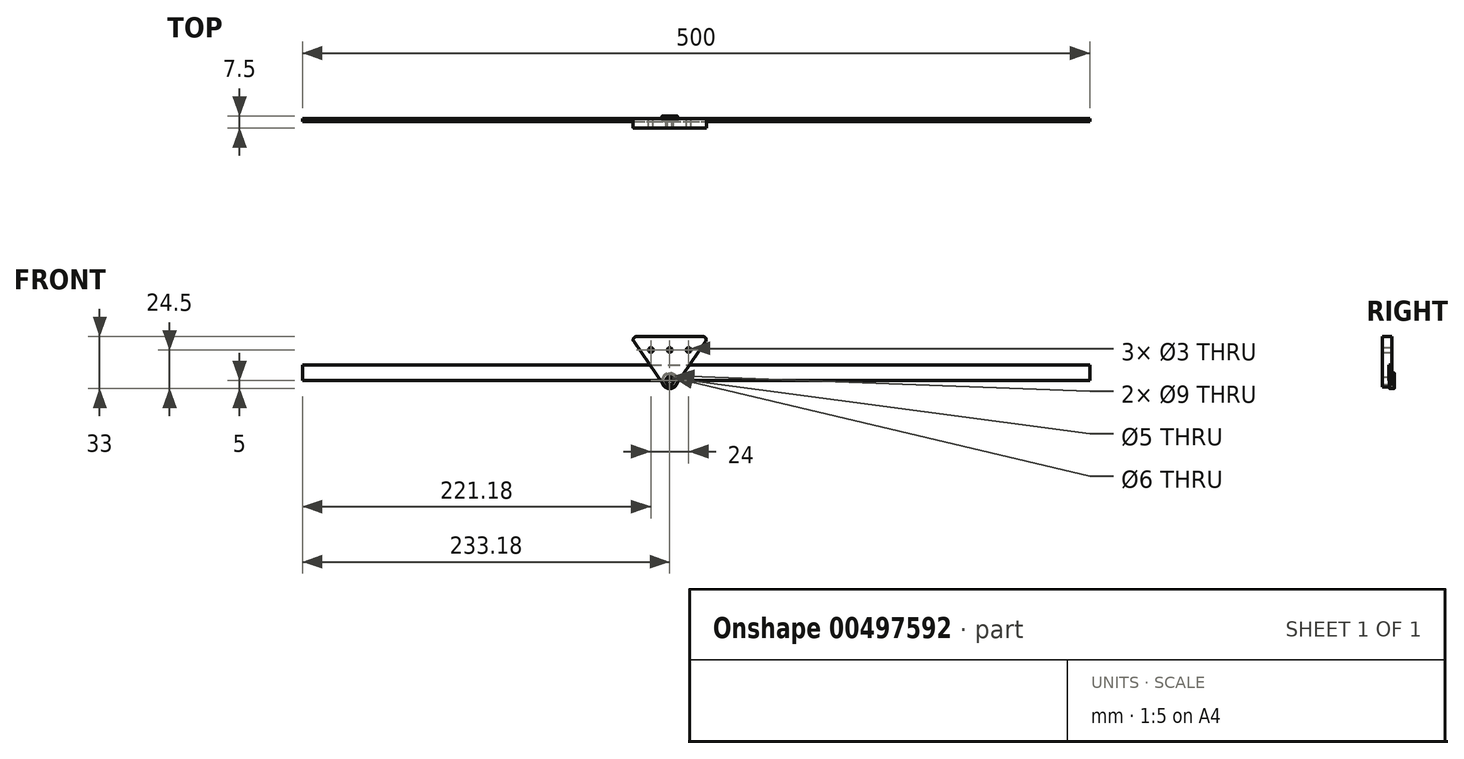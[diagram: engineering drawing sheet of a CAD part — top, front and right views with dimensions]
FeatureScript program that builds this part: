
annotation { "Feature Type Name" : "Feature", "Feature Type Description" : "" }
export const myFeature = defineFeature(function(context is Context, id is Id, definition is map)
    precondition{}
    {
        {
            var Q0;
            Q0=qCreatedBy(makeId("Right.planeOp"),FACE);
            var sketch = newSketch(context, id + "F0", { "sketchPlane" : qUnion([Q0])});
            skLineSegment(sketch, "E0", {"start": v(-1.43, 3.5) * mm, "end": v(-1.47, 3.5) * mm});
            skLineSegment(sketch, "E1", {"start": v(-1.5, 3.47) * mm, "end": v(-1.5, 3.05) * mm});
            skLineSegment(sketch, "E2", {"start": v(-1.45, 3) * mm, "end": v(0, 3) * mm});
            skPoint(sketch, "E3.visualSharp", {"position": v(-1.5, 3) * mm});
            skArc(sketch, "E3.filletArc", {"start": v(-1.5, 3.05) * mm, "mid": v(-1.49, 3.01) * mm, "end": v(-1.45, 3) * mm});
            skPoint(sketch, "E4.visualSharp", {"position": v(-1.5, 3.5) * mm});
            skArc(sketch, "E4.filletArc", {"start": v(-1.47, 3.5) * mm, "mid": v(-1.5, 3.5) * mm, "end": v(-1.5, 3.47) * mm});
            skPoint(sketch, "E5.visualSharp", {"position": v(-1.33, 3.5) * mm});
            skLineSegment(sketch, "E6", {"start": v(-1.33, 4) * mm, "end": v(0.6, 4) * mm, "construction": true});
            skLineSegment(sketch, "E7", {"start": v(-1.33, 3.6) * mm, "end": v(-1.33, 4) * mm});
            skLineSegment(sketch, "E8", {"start": v(-1.33, 3.6) * mm, "end": v(-1.33, 3.53) * mm});
            skLineSegment(sketch, "E9", {"start": v(-1.43, 3.5) * mm, "end": v(-1.36, 3.5) * mm});
            skArc(sketch, "E10.filletArc", {"start": v(-1.36, 3.5) * mm, "mid": v(-1.34, 3.5) * mm, "end": v(-1.33, 3.53) * mm});
            skArc(sketch, "E11.MirrorCS", {"start": v(-1.36, 4.5) * mm, "mid": v(-1.34, 4.5) * mm, "end": v(-1.33, 4.47) * mm});
            skLineSegment(sketch, "E12.MirrorCS", {"start": v(-1.43, 4.5) * mm, "end": v(-1.36, 4.5) * mm});
            skLineSegment(sketch, "E13.MirrorCS", {"start": v(-1.33, 4.4) * mm, "end": v(-1.33, 4.47) * mm});
            skArc(sketch, "E14.MirrorCS", {"start": v(-1.47, 4.5) * mm, "mid": v(-1.5, 4.5) * mm, "end": v(-1.5, 4.53) * mm});
            skLineSegment(sketch, "E15.MirrorCS", {"start": v(-1.43, 4.5) * mm, "end": v(-1.47, 4.5) * mm});
            skArc(sketch, "E16.MirrorCS", {"start": v(-1.5, 4.95) * mm, "mid": v(-1.49, 4.99) * mm, "end": v(-1.45, 5) * mm});
            skPoint(sketch, "E17.MirrorP", {"position": v(-1.33, 4.5) * mm});
            skLineSegment(sketch, "E18.MirrorCS", {"start": v(-1.5, 4.53) * mm, "end": v(-1.5, 4.95) * mm});
            skLineSegment(sketch, "E19.MirrorCS", {"start": v(-1.33, 4.4) * mm, "end": v(-1.33, 4) * mm});
            skPoint(sketch, "E20.MirrorP", {"position": v(-1.5, 5) * mm});
            skPoint(sketch, "E21.MirrorP", {"position": v(-1.5, 4.5) * mm});
            skLineSegment(sketch, "E22", {"start": v(-1.45, 5) * mm, "end": v(0, 5) * mm});
            skLineSegment(sketch, "E23", {"start": v(-5.2, 0) * mm, "end": v(6.02, 0) * mm, "construction": true});
            skLineSegment(sketch, "E24", {"start": v(0, 6.2) * mm, "end": v(0, 1.5) * mm, "construction": true});
            skLineSegment(sketch, "E25.MirrorCS", {"start": v(1.33, 4.4) * mm, "end": v(1.33, 4.47) * mm});
            skArc(sketch, "E26.MirrorCS", {"start": v(1.36, 4.5) * mm, "mid": v(1.34, 4.5) * mm, "end": v(1.33, 4.47) * mm});
            skLineSegment(sketch, "E27.MirrorCS", {"start": v(1.43, 4.5) * mm, "end": v(1.36, 4.5) * mm});
            skLineSegment(sketch, "E28.MirrorCS", {"start": v(1.33, 3.6) * mm, "end": v(1.33, 3.53) * mm});
            skLineSegment(sketch, "E29.MirrorCS", {"start": v(1.43, 3.5) * mm, "end": v(1.36, 3.5) * mm});
            skArc(sketch, "E30.MirrorCS", {"start": v(1.36, 3.5) * mm, "mid": v(1.34, 3.5) * mm, "end": v(1.33, 3.53) * mm});
            skLineSegment(sketch, "E31.MirrorCS", {"start": v(1.43, 3.5) * mm, "end": v(1.47, 3.5) * mm});
            skArc(sketch, "E32.MirrorCS", {"start": v(1.47, 3.5) * mm, "mid": v(1.5, 3.5) * mm, "end": v(1.5, 3.47) * mm});
            skLineSegment(sketch, "E33.MirrorCS", {"start": v(1.43, 4.5) * mm, "end": v(1.47, 4.5) * mm});
            skArc(sketch, "E34.MirrorCS", {"start": v(1.47, 4.5) * mm, "mid": v(1.5, 4.5) * mm, "end": v(1.5, 4.53) * mm});
            skArc(sketch, "E35.MirrorCS", {"start": v(1.5, 3.05) * mm, "mid": v(1.49, 3.01) * mm, "end": v(1.45, 3) * mm});
            skArc(sketch, "E36.MirrorCS", {"start": v(1.5, 4.95) * mm, "mid": v(1.49, 4.99) * mm, "end": v(1.45, 5) * mm});
            skPoint(sketch, "E37.MirrorP", {"position": v(1.33, 3.5) * mm});
            skPoint(sketch, "E38.MirrorP", {"position": v(1.33, 4.5) * mm});
            skLineSegment(sketch, "E39.MirrorCS", {"start": v(1.33, 3.6) * mm, "end": v(1.33, 4) * mm});
            skLineSegment(sketch, "E40.MirrorCS", {"start": v(1.45, 3) * mm, "end": v(0, 3) * mm});
            skLineSegment(sketch, "E41.MirrorCS", {"start": v(1.5, 3.47) * mm, "end": v(1.5, 3.05) * mm});
            skPoint(sketch, "E42.MirrorP", {"position": v(1.5, 3.5) * mm});
            skPoint(sketch, "E43.MirrorP", {"position": v(1.5, 3) * mm});
            skLineSegment(sketch, "E44.MirrorCS", {"start": v(1.45, 5) * mm, "end": v(0, 5) * mm});
            skLineSegment(sketch, "E45.MirrorCS", {"start": v(1.5, 4.53) * mm, "end": v(1.5, 4.95) * mm});
            skLineSegment(sketch, "E46.MirrorCS", {"start": v(1.33, 4.4) * mm, "end": v(1.33, 4) * mm});
            skPoint(sketch, "E47.MirrorP", {"position": v(1.5, 5) * mm});
            skPoint(sketch, "E48.MirrorP", {"position": v(1.5, 4.5) * mm});
            skLineSegment(sketch, "E49.MirrorCS", {"start": v(1.33, 4) * mm, "end": v(-0.6, 4) * mm, "construction": true});
            skSolve(sketch);
        }
        {
            var Q0;
            Q0=qSketchRegion(id+"F0",true);
            var Q1;
            Q1=sQuery(id+"F0.wireOp",EDGE,"E23");
            revolve(context, id + "F1", {"surfaceOperationType" : NewSurfaceOperationType.NEW, "entities" : qUnion([Q0]), "axis" : qUnion([Q1]), "revolveType" : RevolveType.FULL});
        }
        {
            var Q0;
            Q0=qCreatedBy(makeId("Front.planeOp"),FACE);
            var sketch = newSketch(context, id + "F2", { "sketchPlane" : qUnion([Q0])});
            skLineSegment(sketch, "E50", {"start": v(21.08, -5) * mm, "end": v(-21.47, -5) * mm, "construction": true});
            skLineSegment(sketch, "E51", {"start": v(0, -5) * mm, "end": v(0, 28) * mm, "construction": true});
            skLineSegment(sketch, "E52", {"start": v(0, 28) * mm, "end": v(-21.2, 28) * mm});
            skLineSegment(sketch, "E53", {"start": v(-1.95, -4) * mm, "end": v(0, -4) * mm});
            skLineSegment(sketch, "E54", {"start": v(-22.85, 24.87) * mm, "end": v(-3.6, -3.13) * mm});
            skLineSegment(sketch, "E55.MirrorCS", {"start": v(1.95, -4) * mm, "end": v(0, -4) * mm});
            skLineSegment(sketch, "E56.MirrorCS", {"start": v(0, 28) * mm, "end": v(21.2, 28) * mm});
            skLineSegment(sketch, "E57.MirrorCS", {"start": v(22.85, 24.87) * mm, "end": v(3.6, -3.13) * mm});
            skCircle(sketch, "E58", {"center": v(0, 0) * mm, "radius": 2.5 * mm});
            skCircle(sketch, "E59", {"center": v(0, 19.5) * mm, "radius": 1.5 * mm});
            skCircle(sketch, "E60", {"center": v(-12, 19.5) * mm, "radius": 1.5 * mm});
            skCircle(sketch, "E61.MirrorC", {"center": v(12, 19.5) * mm, "radius": 1.5 * mm});
            skPoint(sketch, "E62.visualSharp", {"position": v(-25, 28) * mm});
            skArc(sketch, "E62.filletArc", {"start": v(-21.2, 28) * mm, "mid": v(-22.97, 26.93) * mm, "end": v(-22.85, 24.87) * mm});
            skPoint(sketch, "E63.visualSharp", {"position": v(25, 28) * mm});
            skArc(sketch, "E63.filletArc", {"start": v(22.85, 24.87) * mm, "mid": v(22.97, 26.93) * mm, "end": v(21.2, 28) * mm});
            skPoint(sketch, "E64.visualSharp", {"position": v(3, -4) * mm});
            skArc(sketch, "E64.filletArc", {"start": v(1.95, -4) * mm, "mid": v(2.88, -3.77) * mm, "end": v(3.6, -3.13) * mm});
            skPoint(sketch, "E65.visualSharp", {"position": v(-3, -4) * mm});
            skArc(sketch, "E65.filletArc", {"start": v(-3.6, -3.13) * mm, "mid": v(-2.88, -3.77) * mm, "end": v(-1.95, -4) * mm});
            skSolve(sketch);
        }
        {
            var Q0;
            Q0=makeQuery(id+"F2.imprint","IMPRINT",FACE,{"disambiguationData":[TD([[makeQuery(id+"F2.imprint","IMPRINT",EDGE,{"derivedFrom":sQuery(id+"F2.wireOp",EDGE,"E52")}),1.0]])]});
            extrude(context, id + "F3", {"entities" : qUnion([Q0]), "depth" : 6 * mm, "offsetDistance" : 25 * mm});
        }
        {
            var Q0;
            Q0=qCreatedBy(makeId("Front.planeOp"),FACE);
            var sketch = newSketch(context, id + "F4", { "sketchPlane" : qUnion([Q0])});
            skLineSegment(sketch, "E66.bottom", {"start": v(-233.18, 0) * mm, "end": v(266.82, 0) * mm});
            skLineSegment(sketch, "E66.top", {"start": v(-233.18, 10) * mm, "end": v(266.82, 10) * mm});
            skLineSegment(sketch, "E66.left", {"start": v(-233.18, 0) * mm, "end": v(-233.18, 10) * mm});
            skLineSegment(sketch, "E66.right", {"start": v(266.82, 0) * mm, "end": v(266.82, 10) * mm});
            skSolve(sketch);
        }
        {
            var Q0;
            Q0 = qSketchRegion(id + "F4", true);
            extrude(context, id + "F5", {"entities" : qUnion([Q0]), "depth" : 2 * mm, "offsetDistance" : 25 * mm});
        }
    });
